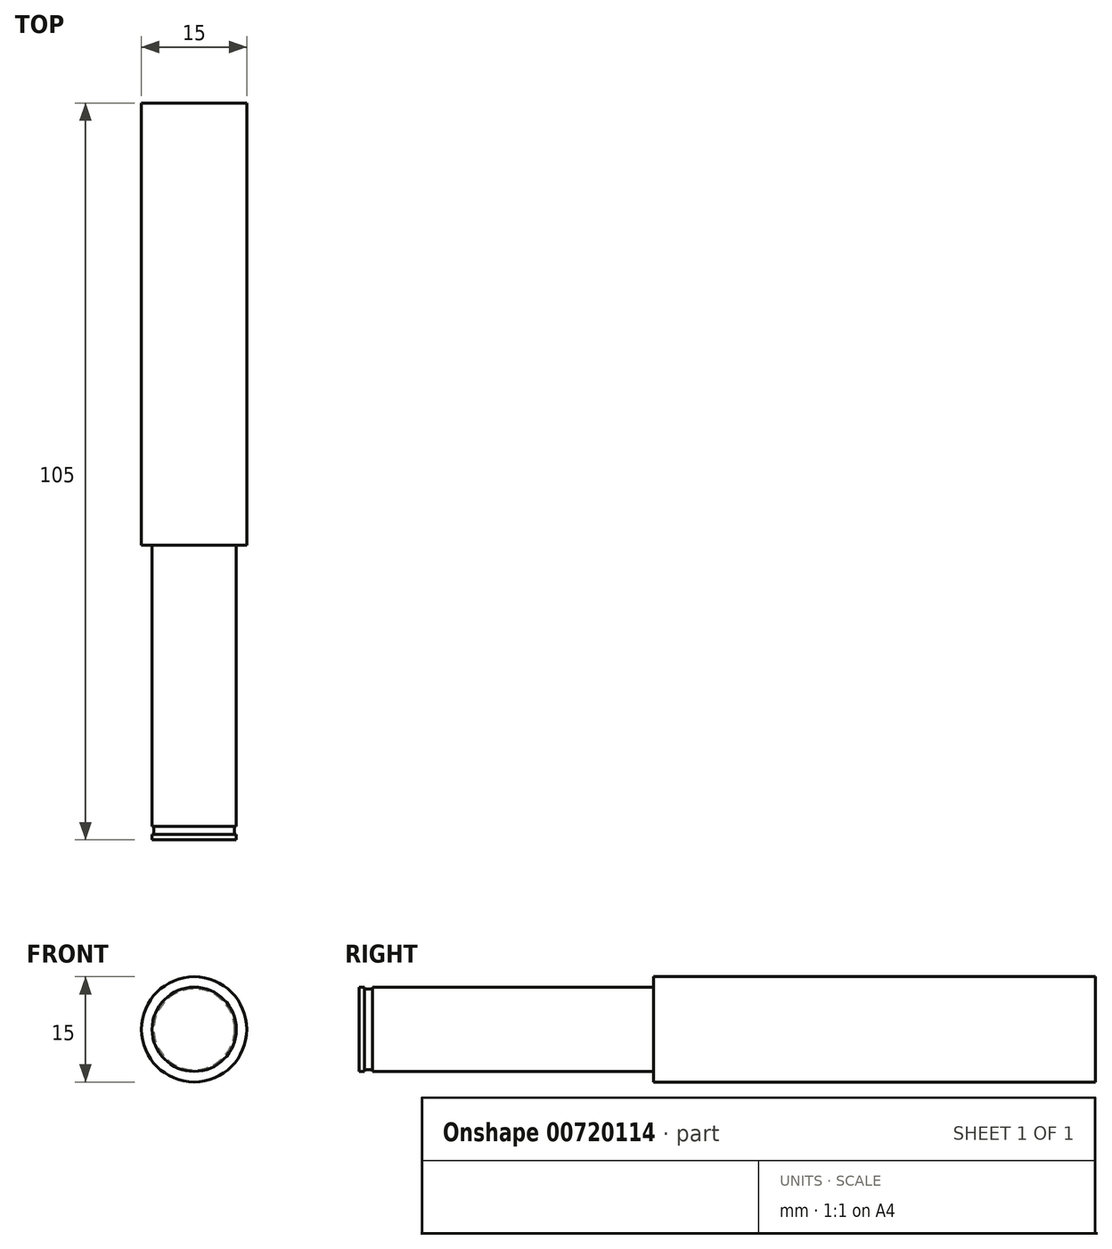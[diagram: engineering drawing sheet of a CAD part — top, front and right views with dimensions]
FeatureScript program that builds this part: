
annotation { "Feature Type Name" : "Feature", "Feature Type Description" : "" }
export const myFeature = defineFeature(function(context is Context, id is Id, definition is map)
    precondition{}
    {
        {
            var Q0;
            Q0=qCreatedBy(makeId("Front.planeOp"),FACE);
            var sketch = newSketch(context, id + "F0", { "sketchPlane" : qUnion([Q0])});
            skCircle(sketch, "E0", {"center": v(0, 0) * mm, "radius": 7.5 * mm});
            skSolve(sketch);
        }
        {
            var Q0;
            Q0=makeQuery(id+"F0.imprint","IMPRINT",FACE,{"disambiguationData":[TD([[makeQuery(id+"F0.imprint","IMPRINT",EDGE,{"derivedFrom":sQuery(id+"F0.wireOp",EDGE,"E0")}),1.0]])]});
            extrude(context, id + "F1", {"entities" : qUnion([Q0]), "depth" : 105 * mm, "offsetDistance" : 25 * mm});
        }
        {
            var Q0;
            Q0=makeQuery(id+"F1.opExtrude","CAP_FACE",FACE,{"disambiguationData":[OSD([sQuery(id+"F0.wireOp",EDGE,"E0")])],"isStart":false});
            var sketch = newSketch(context, id + "F2", { "sketchPlane" : qUnion([Q0])});
            skCircle(sketch, "E1", {"center": v(0, 0) * mm, "radius": 6 * mm});
            skCircle(sketch, "E2", {"center": v(0, 0) * mm, "radius": 7.5 * mm});
            skSolve(sketch);
        }
        {
            var Q0;
            Q0=makeQuery(id+"F2.imprint","IMPRINT",FACE,{"disambiguationData":[TD([[makeQuery(id+"F2.imprint","IMPRINT",EDGE,{"derivedFrom":sQuery(id+"F2.wireOp",EDGE,"E1")}),-1.0]])]});
            extrude(context, id + "F3", {"entities" : qUnion([Q0]), "operationType" : NewBodyOperationType.REMOVE, "oppositeDirection" : true, "depth" : 42 * mm, "offsetDistance" : 25 * mm});
        }
        {
            var Q0;
            Q0=makeQuery(id+"F1.opExtrude","CAP_FACE",FACE,{"disambiguationData":[OSD([sQuery(id+"F0.wireOp",EDGE,"E0")])],"isStart":false});
            cPlane(context, id + "F4", {"entities" : qUnion([Q0]), "cplaneType" : CPlaneType.OFFSET, "offset" : 0.8 * mm, "oppositeDirection" : true, "width" : 150 * mm, "height" : 150 * mm});
        }
        {
            var Q0;
            Q0=qCreatedBy(id+"F4.planeOp",FACE);
            var sketch = newSketch(context, id + "F5", { "sketchPlane" : qUnion([Q0])});
            skCircle(sketch, "E3", {"center": v(0, 0) * mm, "radius": 6 * mm});
            skCircle(sketch, "E4", {"center": v(0, 0) * mm, "radius": 5.75 * mm});
            skSolve(sketch);
        }
        {
            var Q0;
            Q0 = qSketchRegion(id + "F5", true);
            extrude(context, id + "F6", {"entities" : qUnion([Q0]), "operationType" : NewBodyOperationType.REMOVE, "oppositeDirection" : true, "depth" : 1.1 * mm, "offsetDistance" : 25 * mm});
        }
    });
